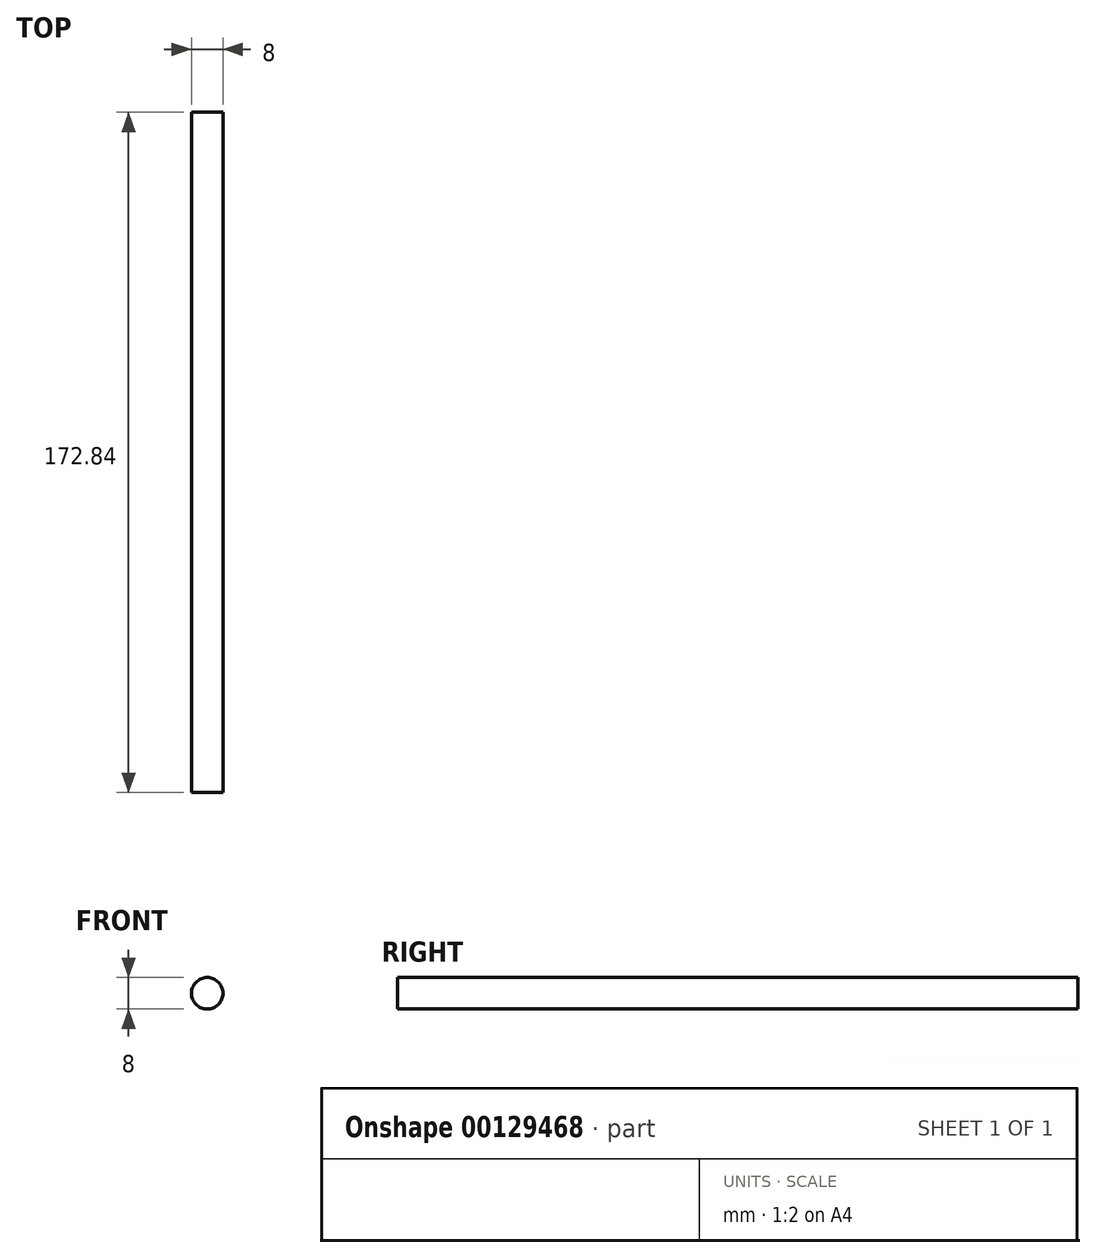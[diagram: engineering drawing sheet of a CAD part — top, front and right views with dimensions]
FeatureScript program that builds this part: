
annotation { "Feature Type Name" : "Feature", "Feature Type Description" : "" }
export const myFeature = defineFeature(function(context is Context, id is Id, definition is map)
    precondition{}
    {
        {
            var Q0;
            Q0=qCreatedBy(makeId("Front.planeOp"),FACE);
            var sketch = newSketch(context, id + "F0", { "sketchPlane" : qUnion([Q0])});
            skCircle(sketch, "E0", {"center": v(0, 0) * mm, "radius": 4 * mm});
            skSolve(sketch);
        }
        {
            var Q0;
            Q0=qSketchRegion(id+"F0",true);
            extrude(context, id + "F1", {"entities" : qUnion([Q0]), "depth" : 172.84 * mm});
        }
    });
